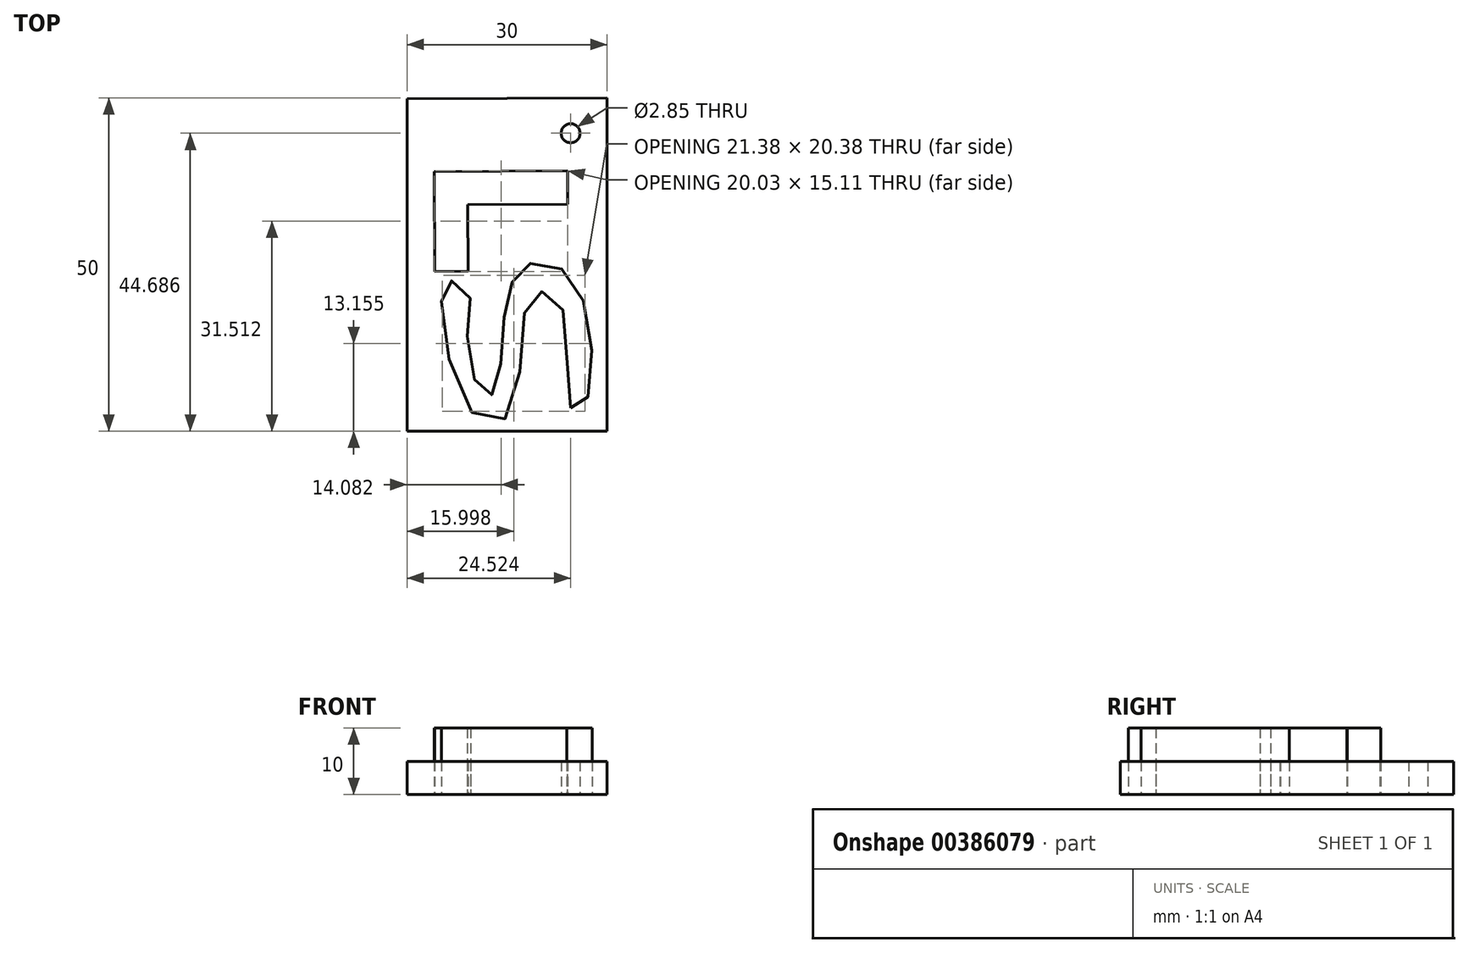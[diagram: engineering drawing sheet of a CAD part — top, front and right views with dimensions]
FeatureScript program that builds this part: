
annotation { "Feature Type Name" : "Feature", "Feature Type Description" : "" }
export const myFeature = defineFeature(function(context is Context, id is Id, definition is map)
    precondition{}
    {
        {
            var Q0;
            Q0=qCreatedBy(makeId("Top.planeOp"),FACE);
            var sketch = newSketch(context, id + "F0", { "sketchPlane" : qUnion([Q0])});
            skLineSegment(sketch, "E0", {"start": v(-75.12, -63.36) * mm, "end": v(-45.12, -63.36) * mm});
            skLineSegment(sketch, "E1", {"start": v(-45.12, -63.36) * mm, "end": v(-45.12, -13.36) * mm});
            skLineSegment(sketch, "E2", {"start": v(-45.12, -13.36) * mm, "end": v(-75.12, -13.53) * mm});
            skLineSegment(sketch, "E3", {"start": v(-75.12, -13.53) * mm, "end": v(-75.12, -63.36) * mm});
            skLineSegment(sketch, "E4", {"start": v(-51.05, -24.3) * mm, "end": v(-71.05, -24.4) * mm});
            skLineSegment(sketch, "E5", {"start": v(-71.05, -24.4) * mm, "end": v(-70.97, -39.4) * mm});
            skLineSegment(sketch, "E6", {"start": v(-70.97, -39.4) * mm, "end": v(-65.97, -39.38) * mm});
            skLineSegment(sketch, "E7", {"start": v(-51.05, -24.3) * mm, "end": v(-51.02, -29.3) * mm});
            skLineSegment(sketch, "E8", {"start": v(-51.02, -29.3) * mm, "end": v(-66.02, -29.38) * mm});
            skLineSegment(sketch, "E9", {"start": v(-66.02, -29.38) * mm, "end": v(-65.97, -39.38) * mm});
            skFitSpline(sketch, "E10", {"points": [v(-50.62, -59.83) * mm, v(-51.4, -46.34) * mm, v(-54.65, -42.45) * mm, v(-57.22, -44.39) * mm, v(-59.67, -60.67) * mm, v(-65.2, -60.76) * mm, v(-69.95, -43.68) * mm, v(-68.77, -40.82) * mm, v(-65.92, -42.55) * mm, v(-66.1, -50.21) * mm, v(-63.58, -57.78) * mm, v(-62.1, -57.6) * mm, v(-60.78, -48.71) * mm, v(-59.34, -40.9) * mm, v(-56.77, -38.24) * mm, v(-51.37, -39.4) * mm, v(-47.67, -48.68) * mm, v(-48.64, -59.49) * mm, v(-50.62, -59.83) * mm]});
            skCircle(sketch, "E11", {"center": v(-50.6, -18.67) * mm, "radius": 1.42 * mm});
            skSolve(sketch);
        }
        {
            var Q0;
            Q0=makeQuery(id+"F0.imprint","IMPRINT",FACE,{"disambiguationData":[TD([[makeQuery(id+"F0.imprint","IMPRINT",EDGE,{"derivedFrom":sQuery(id+"F0.wireOp",EDGE,"E10")}),-1.0]])]});
            var Q1;
            Q1=makeQuery(id+"F0.imprint","IMPRINT",FACE,{"disambiguationData":[TD([[makeQuery(id+"F0.imprint","IMPRINT",EDGE,{"derivedFrom":sQuery(id+"F0.wireOp",EDGE,"E4")}),1.0]])]});
            extrude(context, id + "F1", {"entities" : qUnion([Q0, Q1]), "depth" : 10 * mm});
        }
        {
            var Q0;
            Q0 = qSketchRegion(id + "F0", true);
            extrude(context, id + "F2", {"entities" : qUnion([Q0]), "depth" : 5 * mm});
        }
    });
